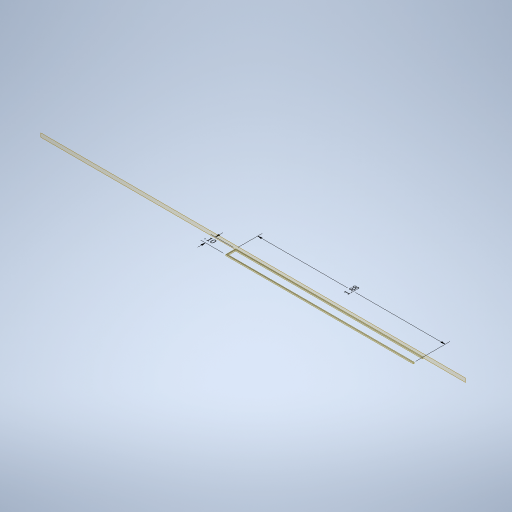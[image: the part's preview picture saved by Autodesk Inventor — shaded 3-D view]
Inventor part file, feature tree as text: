
AUTODESK INVENTOR PART (.ipt)
format: ipt  version: 2024.2 (Build 282272000, 272)  size: 275,456 bytes
history: native  units: in
note: dims shown in document units (in); Inventor stores cm internally (conversion verified against a paired STEP export)
features: other x3, plane x3, sketch x2, sweep x1
ambient origin geometry x8: Origin, YZ Plane, XZ Plane, XY Plane, X Axis, Y Axis, Z Axis, Center Point
bodies: Solid1 (feature_tree)
feature tree (9):
  other  "Annotations"
  sweep  "Sweep1"
  plane  "Work Plane1"
  plane  "Work Plane2"
  plane  "Work Plane4"
  sketch  "Sketch1"  dims[d6=0.0in d7=0.0in d11=0.25in d19=-0.25in]
  sketch  "Sketch2"  dims[d69=1.875in d70=1.875in d86=-0.1175in d89=0.1in d90=0.0in d91=0.0in d92=0.0in d98=0.01in d99=0.01in d100=0.1997in d101=1.875in d102=0.2692in d103=0.1197in d104=0.1in]
  other  "Linear Dimension 1"
  other  "Linear Dimension 2"
